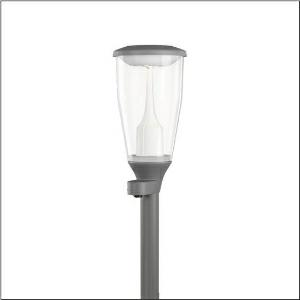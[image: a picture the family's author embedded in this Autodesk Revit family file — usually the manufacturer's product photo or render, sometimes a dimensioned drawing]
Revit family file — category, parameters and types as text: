
# Revit family: dl_11_iq___st1_2a_5xa5575eu14hp00022_2e6b
name_source: partatom
category: Lighting Fixtures
units: mm (PartAtom-declared; Revit-internal decimal feet)

## family parameters
Cut with Voids When Loaded = No
Host = Face
Light Source = No
Part Type = Normal
Room Calculation Point = No
Round Connector Dimension = Use Diameter
Shared = No

## types (1)
- --- (1 x LED, 4790 lm, 33.5 W, 3000K)
    Apparent Load = 34 VA
    CIE Flux Codes = 23 60 93 95 100
    Color Rendering = 70
    Color Temperature = 3000K
    Default Elevation = 1800 mm
    Description = DL 11 iQ, mast luminaire, Module 540 iQ-SR, primary light control with 3 zone facetted reflector, of plastic, silver coated, highly specular, structured, primary optical cover: cover, of PMMA, transparent, light distribution: ST1.2a, light emission: direct distribution, primary light characteristic: asymmetric, installation type: post-top, LED, High Power LED, rated luminous flux: 4.790lm, luminous efficacy: 143lm/W, light colour: 730, colour temperature: 3000K, control gear: iQ-Street Remote, D4i with power reduction, control: pre-setting: logarithmic dimming characteristic, Street-Remote, Auto-Match, Temp-Guard, Lumen-Switch, Night-Set, Smart-Wire, Light-Fading, Desk-Remote (wireless, voltage-free reading and setting of iQ features in the workshop via application-optimized NFC function/RFID function), optimised constant luminous flux control (CLO 2.0), mains connection: 220..240V, AC, 50/60Hz, connection cable pre-assembled, cable length: 5,5m, start of lifetime: 34W, end of service life: 36W, reduction: 15W, luminaire housing, upper part, of diecast aluminium, coated, Siteco® metallic grey (DB 702S), spigot size: 76mm (post-top), mounting height: 3..5m, post-top mast mounting element, of diecast aluminium, coated, Siteco® metallic grey (DB 702S), Module 540 iQ-SR, traffic white (RAL 9016), equipment: Power, Smart Interface below, protection rating (complete): IP66, insulation class (complete): insulation class II (safety insulation), certification: CE, ENEC, ENEC+, VDE, impact resistance: IK07, packaging unit: 1 piece

Light Distribution: ST1.2a
    Height = 665 mm
    Lamp = 1 x LED
    Lamp Light Flux = 4790 lm
    Lamp Power = 33.5 W
    Lamp count = 1
    Length = 334 mm
    Luminous efficacy = 143 lm/W
    Manufacturer = Siteco
    ModVariant = No
    Model = 5XA5575EU14HP00022
    Number of Poles = 1
    OnlyDefault = Yes
    Power Factor = 1
    Product Name = DL 11 iQ | ST1.2a
    Product group = mast luminaire | pylon top
    ProductGroupID = 6100
    Protection Class = Protection class II
    Protection Degree = IP 66
    RLX_Detail_Level = 1
    RLX_Emergency_Light_Flux = 0 lm
    RLX_Emergency_Type = 0
    RLX_Emergency_Type_DB = No
    RlxData = <blob elided: 161613 chars, md5=6e9d8cc0>
    Socket = socket
    Standby Power = 0 W
    System Light Flux = 4790 lm
    System Power = 34 W
    Type Comments = factory setting: luminous flux: 100 % | dim-lin: 254 | 695 mA
    Type Image = l_1337539.jpg
    URL = http://relux.com
    VarID = @adj_033892
    Voltage = 0 V
    Weight = 0.00 kg
    Width = 0 mm  [stored 0 ft]

note: [stored X ft] marks values corroborated as IEEE doubles in the binary element streams (Revit-internal decimal feet)

## geometry (parser evidence)
native form markers: Blend x4, Sweep x13
no freeform markers — native parametric forms only
